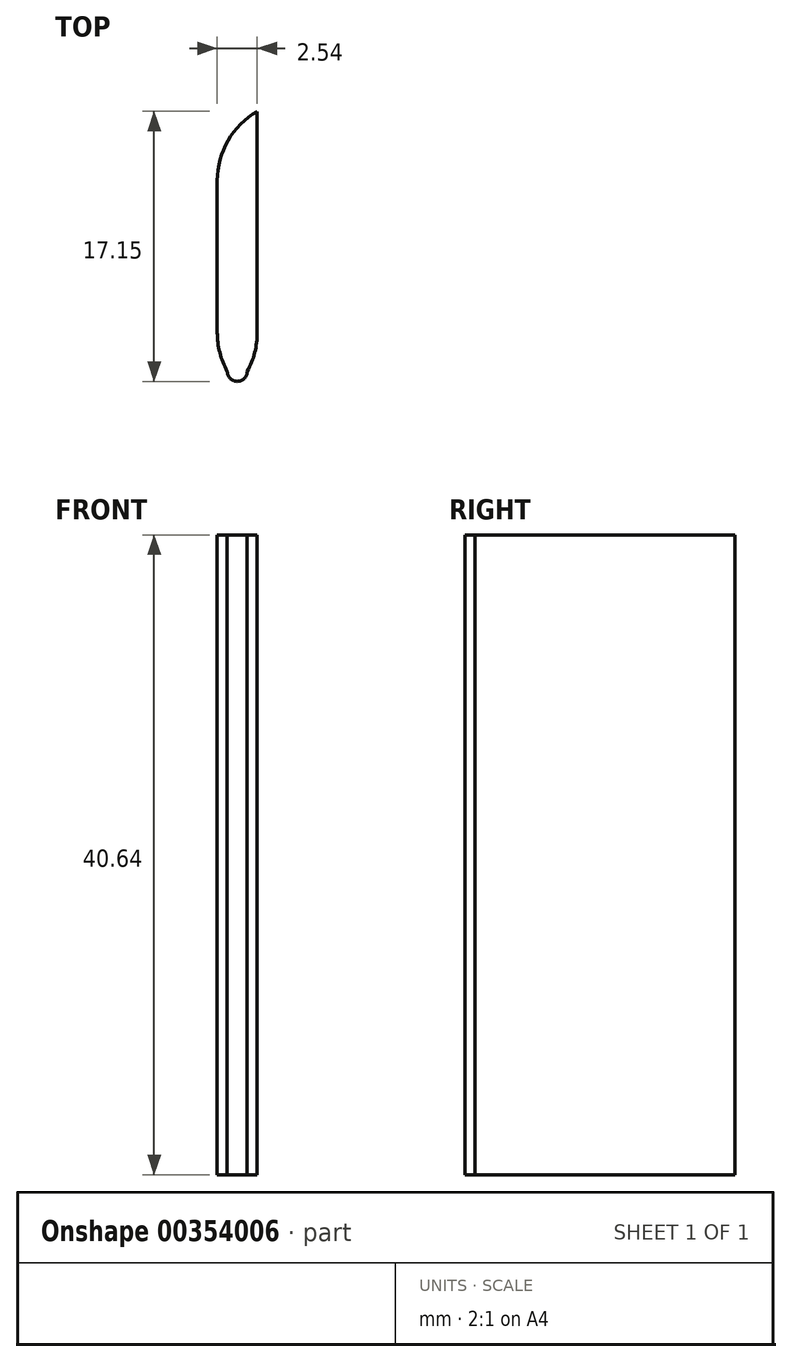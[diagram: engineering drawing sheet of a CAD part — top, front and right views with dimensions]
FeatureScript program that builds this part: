
annotation { "Feature Type Name" : "Feature", "Feature Type Description" : "" }
export const myFeature = defineFeature(function(context is Context, id is Id, definition is map)
    precondition{}
    {
        {
            var Q0;
            Q0=qCreatedBy(makeId("Top.planeOp"),FACE);
            var sketch = newSketch(context, id + "F0", { "sketchPlane" : qUnion([Q0])});
            skLineSegment(sketch, "E0.bottom", {"start": v(1.27, -8.26) * mm, "end": v(-1.27, -8.26) * mm});
            skLineSegment(sketch, "E0.top", {"start": v(1.27, 8.26) * mm, "end": v(-1.27, 8.26) * mm});
            skLineSegment(sketch, "E0.left", {"start": v(1.27, -8.26) * mm, "end": v(1.27, 8.26) * mm});
            skLineSegment(sketch, "E0.right", {"start": v(-1.27, -8.26) * mm, "end": v(-1.27, 8.26) * mm});
            skPoint(sketch, "E0.middle", {"position": v(0, 0) * mm});
            skCircle(sketch, "E1", {"center": v(0, -8.26) * mm, "radius": 0.64 * mm});
            skPoint(sketch, "E1.centerSnap0", {"position": v(0, -8.26) * mm});
            skSolve(sketch);
        }
        {
            var Q0;
            Q0=makeQuery(id+"F0.imprint","IMPRINT",FACE,{"disambiguationData":[TD([[makeQuery(id+"F0.imprint","IMPRINT",EDGE,{"derivedFrom":sQuery(id+"F0.wireOp",EDGE,"E0.top")}),1.0]])]});
            var Q1;
            {var subQ0=sQuery(id+"F0.wireOp",EDGE,"E1");var subQ1=sQuery(id+"F0.wireOp",EDGE,"E0.bottom");var subQ2=makeQuery(id+"F0.imprint","INTERSECT",VERTEX,{"disambiguationData":[OD(0.0)],"derivedFrom":[subQ1,subQ0]});Q1=makeQuery(id+"F0.imprint","IMPRINT",FACE,{"disambiguationData":[TD([[makeQuery(id+"F0.imprint","IMPRINT",EDGE,{"disambiguationData":[TD([[subQ2,-1.0]])],"derivedFrom":subQ1}),1.0]])]});}
            var Q2;
            {var subQ0=sQuery(id+"F0.wireOp",EDGE,"E1");var subQ1=sQuery(id+"F0.wireOp",EDGE,"E0.bottom");var subQ2=makeQuery(id+"F0.imprint","INTERSECT",VERTEX,{"disambiguationData":[OD(0.0)],"derivedFrom":[subQ1,subQ0]});Q2=makeQuery(id+"F0.imprint","IMPRINT",FACE,{"disambiguationData":[TD([[makeQuery(id+"F0.imprint","IMPRINT",EDGE,{"disambiguationData":[TD([[subQ2,-1.0]])],"derivedFrom":subQ1}),-1.0]])]});}
            extrude(context, id + "F1", {"entities" : qUnion([Q0, Q1, Q2]), "depth" : 40.64 * mm});
        }
        {
            var Q0;
            Q0=makeQuery(id+"F1.opExtrude","SWEPT_EDGE",EDGE,{"disambiguationData":[OSD([sQuery(id+"F0.wireOp",EDGE,"E0.top"),sQuery(id+"F0.wireOp",EDGE,"E0.right")])]});
            fillet(context, id + "F2", {"entities" : qUnion([Q0]), "radius" : 5.08 * mm, "tangentPropagation" : true, "allowEdgeOverflow" : false});
        }
        {
            var Q0;
            Q0=makeQuery(id+"F1.opExtrude","SWEPT_EDGE",EDGE,{"disambiguationData":[OSD([sQuery(id+"F0.wireOp",EDGE,"E0.bottom"),sQuery(id+"F0.wireOp",EDGE,"E0.right")])]});
            var Q1;
            Q1=makeQuery(id+"F1.opExtrude","SWEPT_EDGE",EDGE,{"disambiguationData":[OSD([sQuery(id+"F0.wireOp",EDGE,"E0.bottom"),sQuery(id+"F0.wireOp",EDGE,"E0.left")])]});
            fillet(context, id + "F3", {"entities" : qUnion([Q0, Q1]), "radius" : 5.08 * mm, "tangentPropagation" : true, "allowEdgeOverflow" : false});
        }
    });
